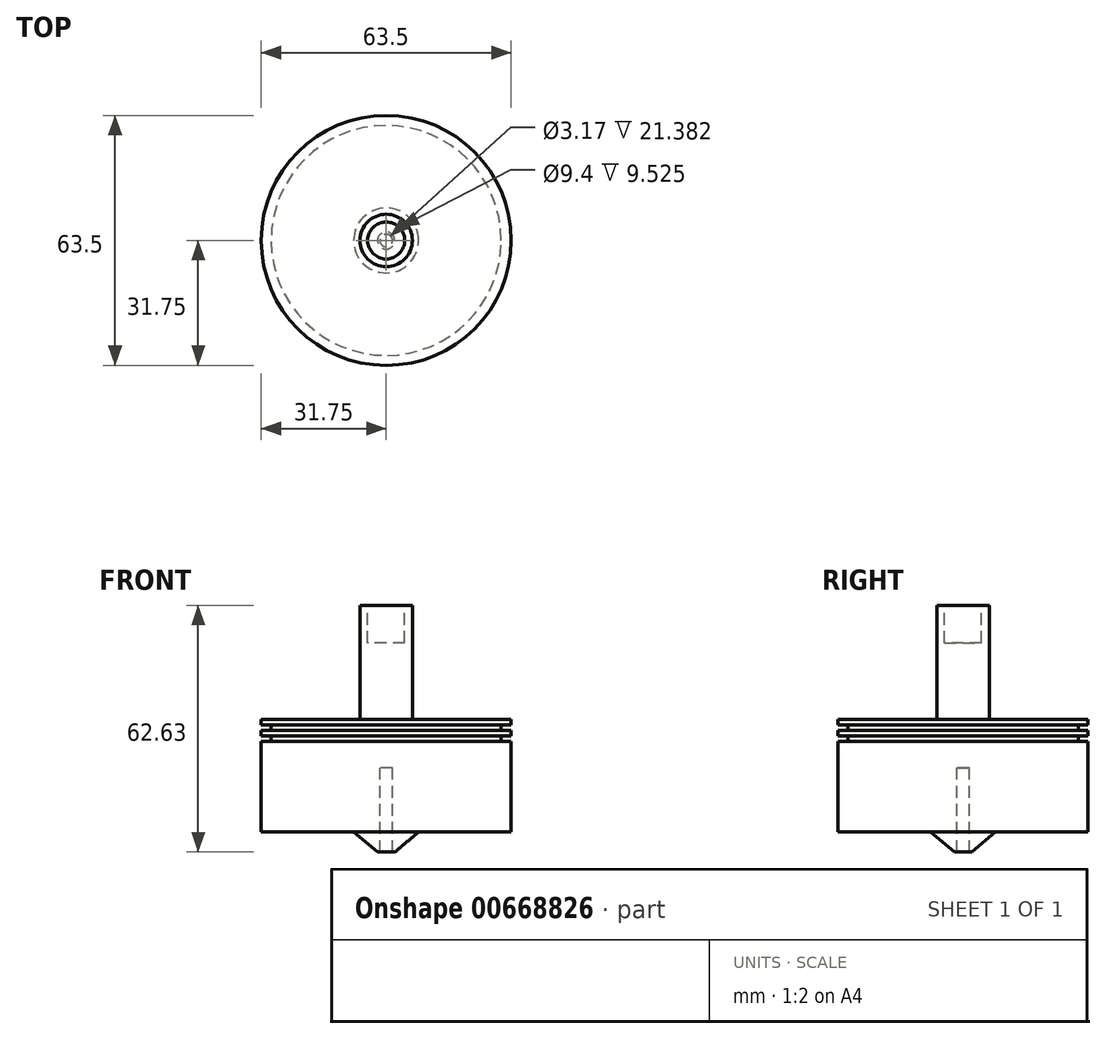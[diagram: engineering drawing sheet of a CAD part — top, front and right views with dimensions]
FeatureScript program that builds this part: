
annotation { "Feature Type Name" : "Feature", "Feature Type Description" : "" }
export const myFeature = defineFeature(function(context is Context, id is Id, definition is map)
    precondition{}
    {
        {
            var Q0;
            Q0=qCreatedBy(makeId("Front.planeOp"),FACE);
            var sketch = newSketch(context, id + "F0", { "sketchPlane" : qUnion([Q0])});
            skLineSegment(sketch, "E0", {"start": v(0.93, -41.48) * mm, "end": v(0.93, -45.57) * mm});
            skLineSegment(sketch, "E1", {"start": v(0.93, -45.57) * mm, "end": v(6.7, -37.79) * mm});
            skLineSegment(sketch, "E2", {"start": v(6.7, -37.79) * mm, "end": v(48.53, -37.79) * mm});
            skLineSegment(sketch, "E3", {"start": v(48.53, -37.79) * mm, "end": v(48.53, -1.2) * mm});
            skLineSegment(sketch, "E4", {"start": v(48.53, -1.2) * mm, "end": v(6.7, -1.2) * mm});
            skLineSegment(sketch, "E5", {"start": v(6.7, -1.2) * mm, "end": v(6.7, 40.56) * mm});
            skLineSegment(sketch, "E6", {"start": v(6.7, 40.56) * mm, "end": v(0.93, 40.56) * mm});
            skLineSegment(sketch, "E7", {"start": v(0.93, 40.56) * mm, "end": v(0.93, -41.48) * mm});
            skSolve(sketch);
        }
        {
            var Q0;
            Q0=qCreatedBy(makeId("Front.planeOp"),FACE);
            var sketch = newSketch(context, id + "F1", { "sketchPlane" : qUnion([Q0])});
            skLineSegment(sketch, "E8", {"start": v(0, 29) * mm, "end": v(0, -34.5) * mm});
            skLineSegment(sketch, "E9", {"start": v(8.26, -28.54) * mm, "end": v(31.75, -28.54) * mm});
            skLineSegment(sketch, "E10", {"start": v(31.75, 0) * mm, "end": v(6.65, 0) * mm});
            skLineSegment(sketch, "E11", {"start": v(6.65, 29) * mm, "end": v(0, 29) * mm});
            skLineSegment(sketch, "E12", {"start": v(1.59, -12.26) * mm, "end": v(0, -12.26) * mm});
            skLineSegment(sketch, "E13", {"start": v(1.59, -12.26) * mm, "end": v(1.59, -33.64) * mm});
            skLineSegment(sketch, "E14", {"start": v(6.65, 29) * mm, "end": v(6.65, 0) * mm});
            skLineSegment(sketch, "E15", {"start": v(31.75, 0) * mm, "end": v(31.75, -1.4) * mm});
            skLineSegment(sketch, "E16", {"start": v(31.75, -1.4) * mm, "end": v(29.22, -1.4) * mm});
            skLineSegment(sketch, "E17", {"start": v(29.22, -1.4) * mm, "end": v(29.22, -2.8) * mm});
            skLineSegment(sketch, "E18", {"start": v(29.22, -2.8) * mm, "end": v(31.75, -2.8) * mm});
            skLineSegment(sketch, "E19", {"start": v(31.75, -2.8) * mm, "end": v(31.75, -4.2) * mm});
            skLineSegment(sketch, "E20", {"start": v(31.75, -4.2) * mm, "end": v(29.22, -4.2) * mm});
            skLineSegment(sketch, "E21", {"start": v(29.22, -4.2) * mm, "end": v(29.22, -5.59) * mm});
            skLineSegment(sketch, "E22", {"start": v(29.22, -5.59) * mm, "end": v(31.75, -5.59) * mm});
            skLineSegment(sketch, "E23", {"start": v(31.75, -5.59) * mm, "end": v(31.75, -28.54) * mm});
            skPoint(sketch, "E24.start.orphan", {"position": v(2.86, -33.64) * mm});
            skLineSegment(sketch, "E25", {"start": v(1.59, -33.64) * mm, "end": v(2.18, -33.64) * mm});
            skLineSegment(sketch, "E26", {"start": v(2.18, -33.64) * mm, "end": v(8.26, -28.54) * mm});
            skSolve(sketch);
        }
        {
            var Q0;
            Q0=makeQuery(id+"F1.imprint","IMPRINT",FACE,{"disambiguationData":[TD([[makeQuery(id+"F1.imprint","IMPRINT",EDGE,{"derivedFrom":sQuery(id+"F1.wireOp",EDGE,"E8")}),1.0]])]});
            var Q1;
            Q1=sQuery(id+"F1.wireOp",EDGE,"E8");
            revolve(context, id + "F2", {"entities" : qUnion([Q0]), "axis" : qUnion([Q1]), "revolveType" : RevolveType.FULL});
        }
        {
            var Q0;
            Q0=makeQuery(id+"F2.opRevolve","SWEPT_FACE",FACE,{"disambiguationData":[OSD([sQuery(id+"F1.wireOp",EDGE,"E11")])]});
            var sketch = newSketch(context, id + "F3", { "sketchPlane" : qUnion([Q0])});
            skCircle(sketch, "E27", {"center": v(0, 0) * mm, "radius": 4.7 * mm});
            skSolve(sketch);
        }
        {
            var Q0;
            Q0=makeQuery(id+"F3.imprint","IMPRINT",FACE,{"disambiguationData":[TD([[makeQuery(id+"F3.imprint","IMPRINT",EDGE,{"derivedFrom":sQuery(id+"F3.wireOp",EDGE,"E27")}),1.0]])]});
            extrude(context, id + "F4", {"entities" : qUnion([Q0]), "operationType" : NewBodyOperationType.REMOVE, "flatOperationType" : FlatOperationType.REMOVE, "oppositeDirection" : true, "depth" : 9.52 * mm, "offsetDistance" : 25.4 * mm, "domain" : OperationDomain.MODEL});
        }
    });
